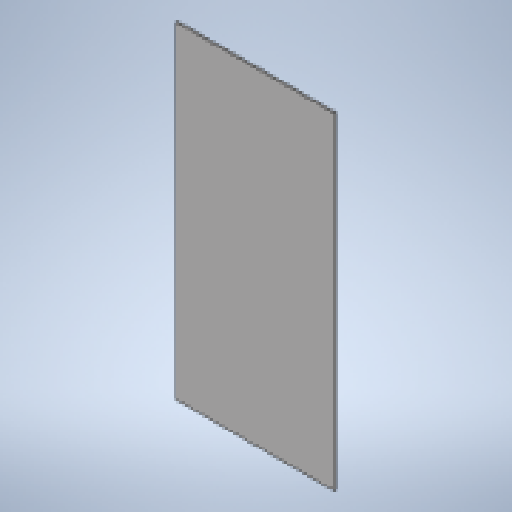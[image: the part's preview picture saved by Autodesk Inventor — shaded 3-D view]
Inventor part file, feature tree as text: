
AUTODESK INVENTOR PART (.ipt)
format: ipt  version: 2025 (Build 290162010, 162A)  size: 146,432 bytes
history: native  units: mm
features: other x2, sheet_metal_op x1, sketch x1
ambient origin geometry x8: Origin, YZ Plane, XZ Plane, XY Plane, X Axis, Y Axis, Z Axis, Center Point
bodies: Body1 (feature_tree)
feature tree (4):
  sheet_metal_op  "Face2"
  sketch  "Sketch1"  dims[d0=400.0mm d1=194.0mm d3=2.0mm]
  other  "Plate2"
  other  "Definition1"
